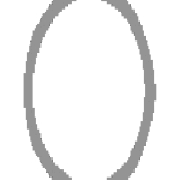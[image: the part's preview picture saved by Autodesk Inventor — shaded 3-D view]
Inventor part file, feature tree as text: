
AUTODESK INVENTOR PART (.ipt)
format: ipt  version: 2021 (Build 250183000, 183)  size: 119,808 bytes
history: native  units: in
note: dims shown in document units (in); Inventor stores cm internally (conversion verified against a paired STEP export)
features: other x4, plane x3, sketch x3, split x2
ambient origin geometry x8: Origin, YZ Plane, XZ Plane, XY Plane, X Axis, Y Axis, Z Axis, Center Point
bodies: Solid1 (feature_tree), Body (feature_tree)
feature tree (12):
  other  "Driven Length"
  other  "Frame Generator"
  other  "Start Plane"
  other  "End Plane"
  plane  "Work Plane5"
  split  "Split1"
  plane  "Work Plane6"
  split  "Split2"
  sketch  "Sketch"  dims[d2=13.0in d4=-0.0in d5=13.3536in d6=0.12in d7=0.0in d10=90.0deg d9=13.3536in]
  sketch  "Sketch4"  dims[d0=1.0in]
  plane  "Work Plane4"
  sketch  "Sketch5"  dims[d1=0.065in]
